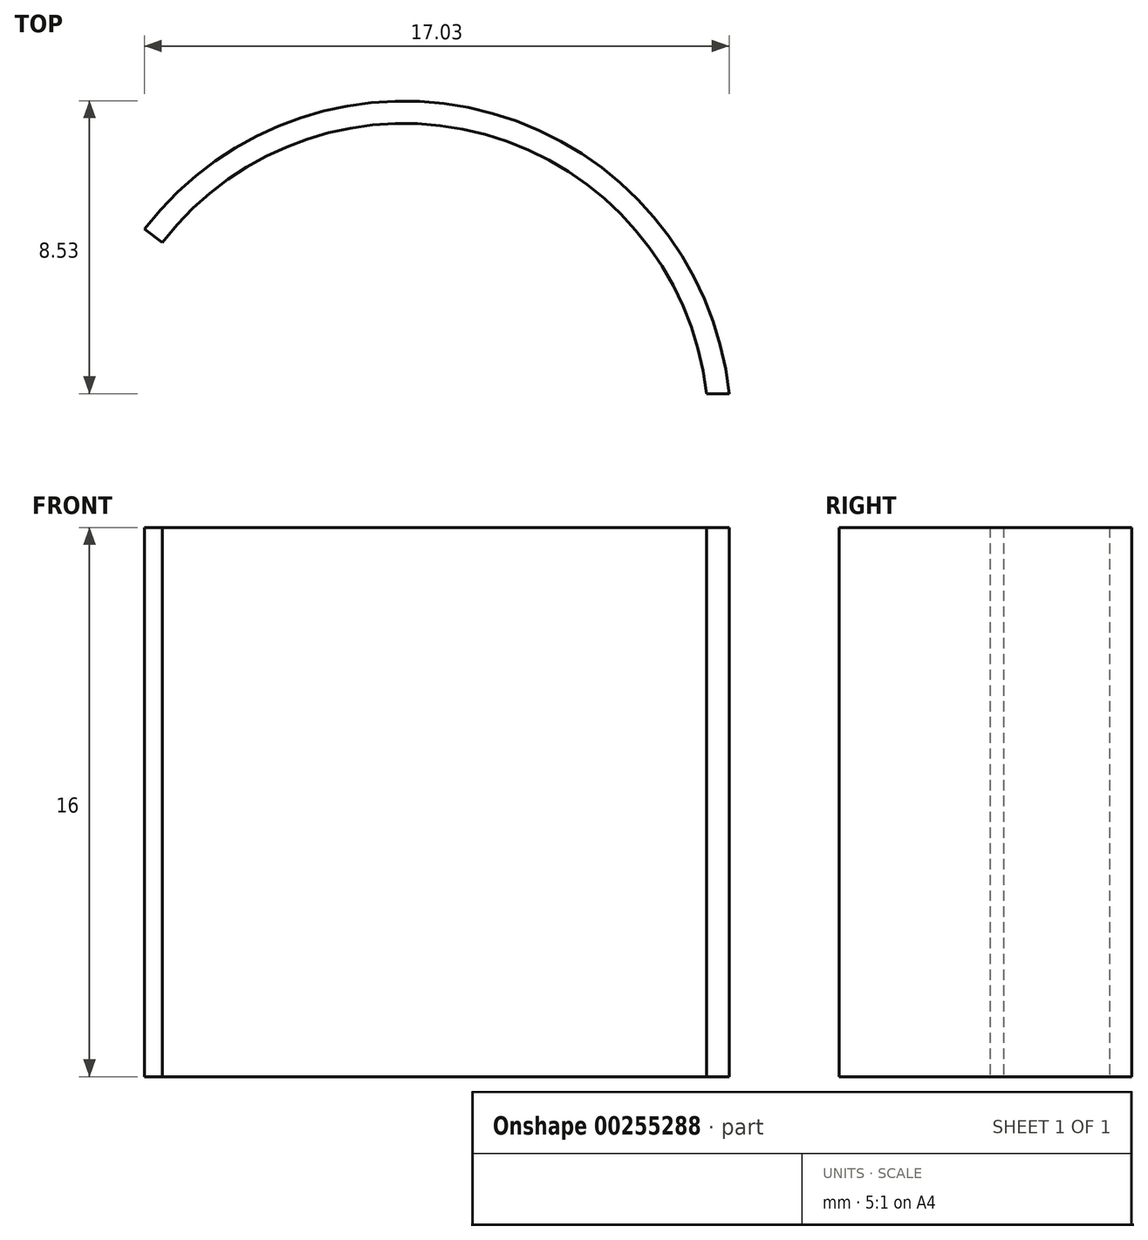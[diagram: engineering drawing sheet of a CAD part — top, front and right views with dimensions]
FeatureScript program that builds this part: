
annotation { "Feature Type Name" : "Feature", "Feature Type Description" : "" }
export const myFeature = defineFeature(function(context is Context, id is Id, definition is map)
    precondition{}
    {
        {
            var Q0;
            Q0=qCreatedBy(makeId("Top.planeOp"),FACE);
            var sketch = newSketch(context, id + "F0", { "sketchPlane" : qUnion([Q0])});
            skCircle(sketch, "E0", {"center": v(0, 0) * mm, "radius": 9.53 * mm});
            skLineSegment(sketch, "E1", {"start": v(-9.12, 7) * mm, "end": v(0, 0) * mm});
            skLineSegment(sketch, "E2", {"start": v(0, 0) * mm, "end": v(-9.12, -7) * mm});
            skLineSegment(sketch, "E3", {"start": v(11.46, 1) * mm, "end": v(9.47, 1) * mm});
            skLineSegment(sketch, "E4", {"start": v(11.46, -1) * mm, "end": v(9.47, -1) * mm});
            skCircle(sketch, "E5", {"center": v(0, 0) * mm, "radius": 11.5 * mm});
            skPoint(sketch, "E6", {"position": v(23.92, 0) * mm});
            skLineSegment(sketch, "E7", {"start": v(23.92, 0) * mm, "end": v(5.53, 10.08) * mm});
            skLineSegment(sketch, "E8", {"start": v(23.92, 0) * mm, "end": v(5.53, -10.08) * mm});
            skPoint(sketch, "E9", {"position": v(19.92, 0) * mm});
            skLineSegment(sketch, "E10", {"start": v(19.92, 0) * mm, "end": v(10.19, 5.34) * mm});
            skLineSegment(sketch, "E11", {"start": v(19.92, 0) * mm, "end": v(10.19, -5.34) * mm});
            skLineSegment(sketch, "E12", {"start": v(19.92, 0) * mm, "end": v(45.5, -14.02) * mm});
            skLineSegment(sketch, "E13", {"start": v(23.92, 0) * mm, "end": v(46.42, -12.33) * mm});
            skLineSegment(sketch, "E14", {"start": v(45.5, -14.02) * mm, "end": v(46.42, -12.33) * mm});
            skLineSegment(sketch, "E15", {"start": v(19.92, 0) * mm, "end": v(21.92, 1.1) * mm});
            skCircle(sketch, "E16", {"center": v(0, 0) * mm, "radius": 8.87 * mm});
            skLineSegment(sketch, "E17", {"start": v(8.82, 1) * mm, "end": v(11.46, 1) * mm});
            skLineSegment(sketch, "E18", {"start": v(8.82, -1) * mm, "end": v(11.46, -1) * mm});
            skPoint(sketch, "E19", {"position": v(-7.56, 5.8) * mm});
            skPoint(sketch, "E20", {"position": v(-7.04, 5.4) * mm});
            skPoint(sketch, "E21", {"position": v(-7.56, -5.8) * mm});
            skPoint(sketch, "E22", {"position": v(-7.04, -5.4) * mm});
            skSolve(sketch);
        }
        {
            var Q0;
            {var subQ0=sQuery(id+"F0.wireOp",EDGE,"E1");var subQ1=sQuery(id+"F0.wireOp",EDGE,"E0");var subQ2=makeQuery(id+"F0.imprint","INTERSECT",VERTEX,{"derivedFrom":[subQ1,subQ0]});Q0=makeQuery(id+"F0.imprint","IMPRINT",FACE,{"disambiguationData":[TD([[makeQuery(id+"F0.imprint","IMPRINT",EDGE,{"disambiguationData":[TD([[subQ2,1.0]])],"derivedFrom":subQ1}),1.0]])]});}
            extrude(context, id + "F1", {"entities" : qUnion([Q0]), "endBound" : BoundingType.SYMMETRIC, "depth" : 16 * mm});
        }
    });
